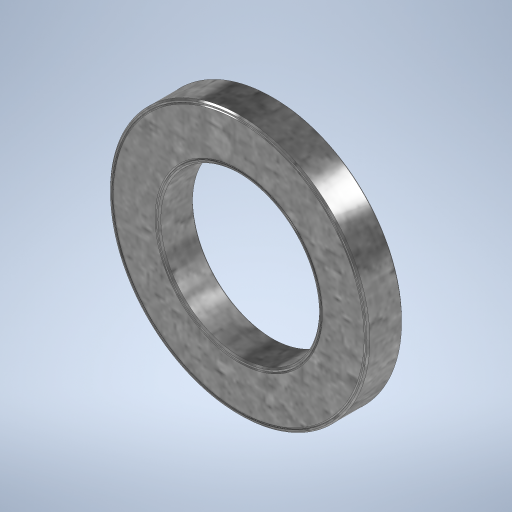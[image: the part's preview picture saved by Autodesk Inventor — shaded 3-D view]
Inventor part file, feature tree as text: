
AUTODESK INVENTOR PART (.ipt)
format: ipt  version: 2023 (Build 270158000, 158)  size: 398,336 bytes
history: native  units: mm
features: sketch x2, other x1, extrude x1, chamfer x1, revolve x1
ambient origin geometry x8: Origin, YZ Plane, XZ Plane, XY Plane, X Axis, Y Axis, Z Axis, Center Point
bodies: Body1 (feature_tree)
feature tree (6):
  other  "솔리드1"
  extrude  "돌출1"  Depth=55.0mm
  chamfer  "모따기1"  Distance=90.0mm
  revolve  "회전1"
  sketch  "스케치1"
  sketch  "스케치2"
